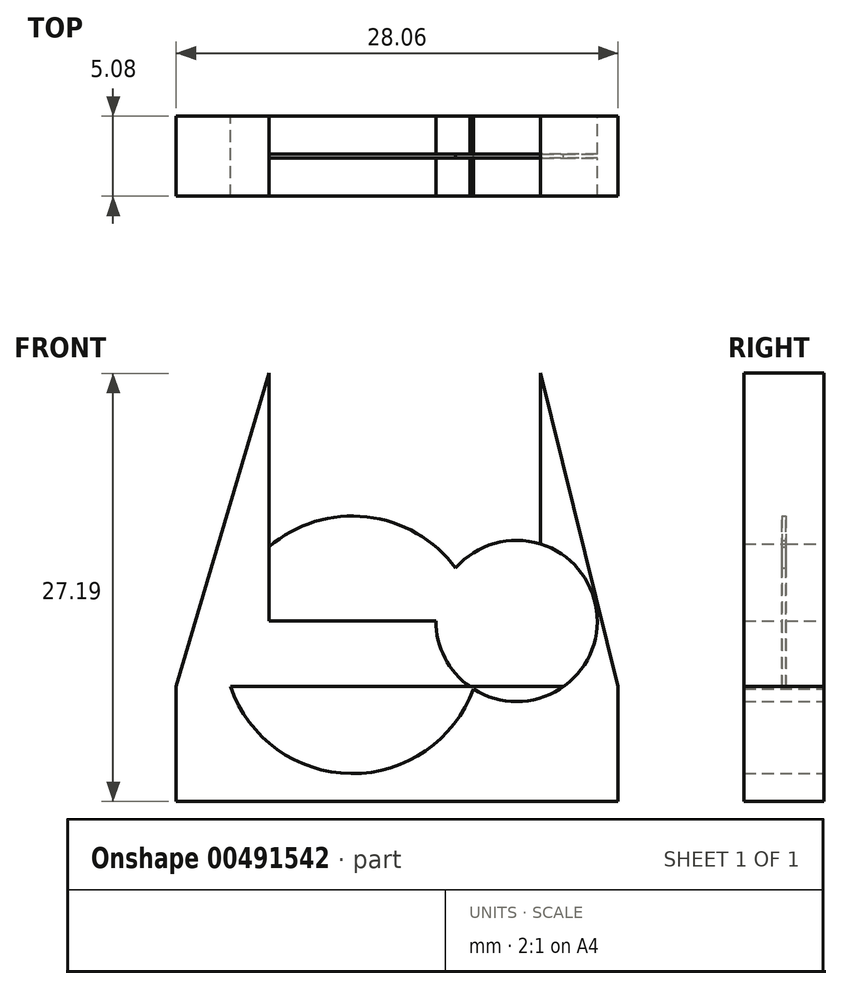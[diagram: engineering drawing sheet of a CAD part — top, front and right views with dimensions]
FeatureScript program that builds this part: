
annotation { "Feature Type Name" : "Feature", "Feature Type Description" : "" }
export const myFeature = defineFeature(function(context is Context, id is Id, definition is map)
    precondition{}
    {
        {
            var Q0;
            Q0=qCreatedBy(makeId("Front.planeOp"),FACE);
            var sketch = newSketch(context, id + "F0", { "sketchPlane" : qUnion([Q0])});
            skLineSegment(sketch, "E0.bottom", {"start": v(-10.48, 0) * mm, "end": v(17.58, 0) * mm});
            skLineSegment(sketch, "E0.top", {"start": v(-10.48, 7.28) * mm, "end": v(17.58, 7.28) * mm});
            skLineSegment(sketch, "E0.left", {"start": v(-10.48, 0) * mm, "end": v(-10.48, 7.28) * mm});
            skLineSegment(sketch, "E0.right", {"start": v(17.58, 0) * mm, "end": v(17.58, 7.28) * mm});
            skLineSegment(sketch, "E1", {"start": v(-10.48, 7.28) * mm, "end": v(-4.6, 27.2) * mm});
            skLineSegment(sketch, "E2", {"start": v(-4.6, 27.2) * mm, "end": v(-4.6, 11.46) * mm});
            skLineSegment(sketch, "E3", {"start": v(0.7, 11.46) * mm, "end": v(-4.6, 11.46) * mm});
            skLineSegment(sketch, "E4", {"start": v(0.7, 11.46) * mm, "end": v(11.14, 11.46) * mm});
            skLineSegment(sketch, "E5", {"start": v(12.65, 11.46) * mm, "end": v(12.65, 27.2) * mm});
            skLineSegment(sketch, "E6", {"start": v(17.58, 7.28) * mm, "end": v(12.65, 27.2) * mm});
            skCircle(sketch, "E7", {"center": v(11.14, 11.46) * mm, "radius": 5.12 * mm});
            skCircle(sketch, "E8", {"center": v(0.7, 9.94) * mm, "radius": 8.18 * mm});
            skSolve(sketch);
        }
        {
            var Q0;
            {var subQ0=sQuery(id+"F0.wireOp",EDGE,"E6");Q0=makeQuery(id+"F0.imprint","IMPRINT",FACE,{"disambiguationData":[TD([[makeQuery(id+"F0.imprint","IMPRINT",EDGE,{"derivedFrom":subQ0}),1.0]])]});}
            var Q1;
            {var subQ0=sQuery(id+"F0.wireOp",EDGE,"E1");Q1=makeQuery(id+"F0.imprint","IMPRINT",FACE,{"disambiguationData":[TD([[makeQuery(id+"F0.imprint","IMPRINT",EDGE,{"derivedFrom":subQ0}),-1.0]])]});}
            var Q2;
            {var subQ0=sQuery(id+"F0.wireOp",EDGE,"E3");Q2=makeQuery(id+"F0.imprint","IMPRINT",FACE,{"disambiguationData":[TD([[makeQuery(id+"F0.imprint","IMPRINT",EDGE,{"derivedFrom":subQ0}),1.0]])]});}
            var Q3;
            {var subQ0=sQuery(id+"F0.wireOp",EDGE,"E0.right");Q3=makeQuery(id+"F0.imprint","IMPRINT",FACE,{"disambiguationData":[TD([[makeQuery(id+"F0.imprint","IMPRINT",EDGE,{"derivedFrom":subQ0}),1.0]])]});}
            var Q4;
            {var subQ0=sQuery(id+"F0.wireOp",EDGE,"E0.left");Q4=makeQuery(id+"F0.imprint","IMPRINT",FACE,{"disambiguationData":[TD([[makeQuery(id+"F0.imprint","IMPRINT",EDGE,{"derivedFrom":subQ0}),-1.0]])]});}
            var Q5;
            {var subQ0=sQuery(id+"F0.wireOp",EDGE,"E8");var subQ1=sQuery(id+"F0.wireOp",EDGE,"E0.bottom");var subQ2=makeQuery(id+"F0.imprint","INTERSECT",VERTEX,{"disambiguationData":[OD(0.0)],"derivedFrom":[subQ1,subQ0]});Q5=makeQuery(id+"F0.imprint","IMPRINT",FACE,{"disambiguationData":[TD([[makeQuery(id+"F0.imprint","IMPRINT",EDGE,{"disambiguationData":[TD([[subQ2,-1.0]])],"derivedFrom":subQ1}),1.0]])]});}
            extrude(context, id + "F1", {"entities" : qUnion([Q0, Q1, Q2, Q3, Q4, Q5]), "endBound" : BoundingType.SYMMETRIC, "depth" : 5.08 * mm});
        }
        {
            var Q0;
            {var subQ5=sQuery(id+"F0.wireOp",EDGE,"E3");Q0=makeQuery(id+"F0.imprint","IMPRINT",FACE,{"disambiguationData":[TD([[makeQuery(id+"F0.imprint","IMPRINT",EDGE,{"derivedFrom":subQ5}),-1.0]])]});}
            var Q1;
            {var subQ0=sQuery(id+"F0.wireOp",EDGE,"E8");var subQ1=sQuery(id+"F0.wireOp",EDGE,"E4");var subQ2=makeQuery(id+"F0.imprint","INTERSECT",VERTEX,{"derivedFrom":[subQ1,subQ0]});Q1=makeQuery(id+"F0.imprint","IMPRINT",FACE,{"disambiguationData":[TD([[makeQuery(id+"F0.imprint","IMPRINT",EDGE,{"disambiguationData":[TD([[subQ2,1.0]])],"derivedFrom":subQ1}),1.0]])]});}
            var Q2;
            {var subQ0=sQuery(id+"F0.wireOp",EDGE,"E7");var subQ1=sQuery(id+"F0.wireOp",EDGE,"E0.top");var subQ2=makeQuery(id+"F0.imprint","INTERSECT",VERTEX,{"disambiguationData":[OD(0.0)],"derivedFrom":[subQ1,subQ0]});Q2=makeQuery(id+"F0.imprint","IMPRINT",FACE,{"disambiguationData":[TD([[makeQuery(id+"F0.imprint","IMPRINT",EDGE,{"disambiguationData":[TD([[subQ2,-1.0]])],"derivedFrom":subQ1}),1.0]])]});}
            var Q3;
            {var subQ0=sQuery(id+"F0.wireOp",EDGE,"E8");var subQ5=sQuery(id+"F0.wireOp",EDGE,"E0.top");var subQ7=makeQuery(id+"F0.imprint","INTERSECT",VERTEX,{"disambiguationData":[OD(1.0)],"derivedFrom":[subQ5,subQ0]});Q3=makeQuery(id+"F0.imprint","IMPRINT",FACE,{"disambiguationData":[TD([[makeQuery(id+"F0.imprint","IMPRINT",EDGE,{"disambiguationData":[TD([[subQ7,-1.0]])],"derivedFrom":subQ5}),1.0]])]});}
            extrude(context, id + "F2", {"entities" : qUnion([Q0, Q1, Q2, Q3]), "operationType" : NewBodyOperationType.ADD, "endBound" : BoundingType.SYMMETRIC, "depth" : 0.25 * mm});
        }
    });
